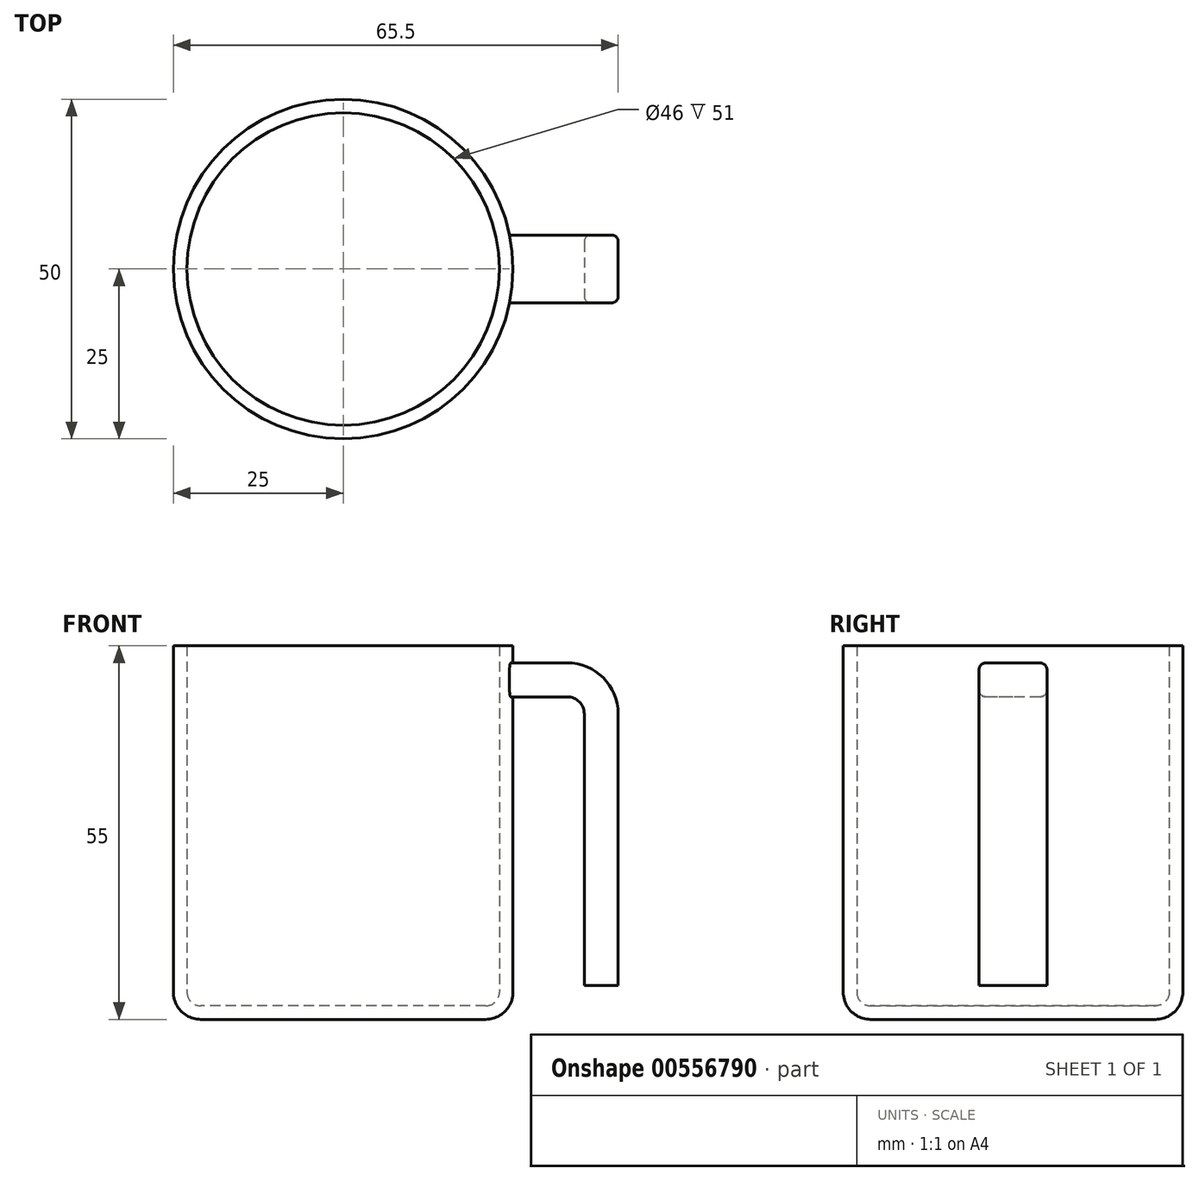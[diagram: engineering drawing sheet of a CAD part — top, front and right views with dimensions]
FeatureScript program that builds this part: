
annotation { "Feature Type Name" : "Feature", "Feature Type Description" : "" }
export const myFeature = defineFeature(function(context is Context, id is Id, definition is map)
    precondition{}
    {
        {
            var Q0;
            Q0=qCreatedBy(makeId("Top.planeOp"),FACE);
            var sketch = newSketch(context, id + "F0", { "sketchPlane" : qUnion([Q0])});
            skCircle(sketch, "E0", {"center": v(0, 0) * mm, "radius": 25 * mm});
            skSolve(sketch);
        }
        {
            var Q0;
            Q0 = qSketchRegion(id + "F0", true);
            extrude(context, id + "F1", {"entities" : qUnion([Q0]), "depth" : 55 * mm, "offsetDistance" : 25 * mm});
        }
        {
            var Q0;
            Q0=makeQuery(id+"F1.opExtrude","CAP_FACE",FACE,{"disambiguationData":[OSD([sQuery(id+"F0.wireOp",EDGE,"E0")])],"isStart":false});
            shell(context, id + "F2", {"entities" : qUnion([Q0]), "thickness" : 2 * mm});
        }
        {
            var Q0;
            Q0=makeQuery(id+"F1.opExtrude","CAP_EDGE",EDGE,{"disambiguationData":[OSD([sQuery(id+"F0.wireOp",EDGE,"E0")])],"isStart":true});
            fillet(context, id + "F3", {"entities" : qUnion([Q0]), "radius" : 4 * mm, "tangentPropagation" : true, "allowEdgeOverflow" : false});
        }
        {
            var Q0;
            Q0=qCreatedBy(makeId("Front.planeOp"),FACE);
            var sketch = newSketch(context, id + "F4", { "sketchPlane" : qUnion([Q0])});
            skLineSegment(sketch, "E1", {"start": v(0, 50) * mm, "end": v(33, 50) * mm});
            skLineSegment(sketch, "E2", {"start": v(38, 45) * mm, "end": v(38, 5) * mm});
            skPoint(sketch, "E3.visualSharp", {"position": v(38, 50) * mm});
            skArc(sketch, "E3.filletArc", {"start": v(38, 45) * mm, "mid": v(36.54, 48.54) * mm, "end": v(33, 50) * mm});
            skSolve(sketch);
        }
        {
            var Q0;
            Q0=qCreatedBy(makeId("Right.planeOp"),FACE);
            var sketch = newSketch(context, id + "F5", { "sketchPlane" : qUnion([Q0])});
            skLineSegment(sketch, "E4.bottom", {"start": v(4, 52.5) * mm, "end": v(-4, 52.5) * mm});
            skLineSegment(sketch, "E4.top", {"start": v(4, 47.5) * mm, "end": v(-4, 47.5) * mm});
            skLineSegment(sketch, "E4.left", {"start": v(5, 51.5) * mm, "end": v(5, 48.5) * mm});
            skLineSegment(sketch, "E4.right", {"start": v(-5, 51.5) * mm, "end": v(-5, 48.5) * mm});
            skPoint(sketch, "E4.middle", {"position": v(0, 50) * mm});
            skPoint(sketch, "E5.visualSharp", {"position": v(5, 52.5) * mm});
            skArc(sketch, "E5.filletArc", {"start": v(5, 51.5) * mm, "mid": v(4.7, 52.2) * mm, "end": v(4, 52.5) * mm});
            skPoint(sketch, "E6.visualSharp", {"position": v(5, 47.5) * mm});
            skArc(sketch, "E6.filletArc", {"start": v(4, 47.5) * mm, "mid": v(4.7, 47.8) * mm, "end": v(5, 48.5) * mm});
            skPoint(sketch, "E7.visualSharp", {"position": v(-5, 47.5) * mm});
            skArc(sketch, "E7.filletArc", {"start": v(-5, 48.5) * mm, "mid": v(-4.7, 47.8) * mm, "end": v(-4, 47.5) * mm});
            skPoint(sketch, "E8.visualSharp", {"position": v(-5, 52.5) * mm});
            skArc(sketch, "E8.filletArc", {"start": v(-4, 52.5) * mm, "mid": v(-4.7, 52.2) * mm, "end": v(-5, 51.5) * mm});
            skSolve(sketch);
        }
        {
            var Q0;
            Q0 = qSketchRegion(id + "F5", true);
            var Q1;
            Q1 = qConstructionFilter(qBodyType(qCreatedBy(id + "F4" ,EDGE), BodyType.WIRE), ConstructionObject.NO);
            sweep(context, id + "F6", {"operationType" : NewBodyOperationType.ADD, "profiles" : qUnion([Q0]), "path" : qUnion([Q1])});
        }
        {
            var Q0;
            Q0=makeQuery(id+"F6.opSweep","CAP_FACE",FACE,{"disambiguationData":[OSD([sQuery(id+"F4.wireOp",VERTEX,"E1.start"),sQuery(id+"F5.wireOp",EDGE,"E4.bottom"),sQuery(id+"F5.wireOp",EDGE,"E4.top"),sQuery(id+"F5.wireOp",EDGE,"E4.left"),sQuery(id+"F5.wireOp",EDGE,"E4.right"),sQuery(id+"F5.wireOp",EDGE,"E5.filletArc"),sQuery(id+"F5.wireOp",EDGE,"E6.filletArc"),sQuery(id+"F5.wireOp",EDGE,"E7.filletArc"),sQuery(id+"F5.wireOp",EDGE,"E8.filletArc")])],"isStart":true});
            var Q1;
            {var subQ0=sQuery(id+"F0.wireOp",EDGE,"E0");Q1=makeQuery(id+"F2.opShell","OFFSET_FACE",FACE,{"disambiguationData":[OSD([subQ0]),TDD([makeQuery(id+"F1.opExtrude","SWEPT_FACE",FACE,{"disambiguationData":[OSD([subQ0])]})])]});}
            extrude(context, id + "F7", {"entities" : qUnion([Q0]), "operationType" : NewBodyOperationType.REMOVE, "endBound" : BoundingType.UP_TO_SURFACE, "oppositeDirection" : true, "depth" : 25 * mm, "endBoundEntityFace" : qUnion([Q1]), "offsetDistance" : 25 * mm});
        }
        {
            var Q0;
            {var subQ0=sQuery(id+"F0.wireOp",EDGE,"E0");Q0=makeQuery(id+"F2.opShell","OFFSET_FACE",FACE,{"disambiguationData":[OSD([subQ0]),TDD([makeQuery(id+"F1.opExtrude","CAP_FACE",FACE,{"disambiguationData":[OSD([subQ0])],"isStart":true})])]});}
            fillet(context, id + "F8", {"entities" : qUnion([Q0]), "radius" : 2 * mm, "tangentPropagation" : true, "allowEdgeOverflow" : false});
        }
    });
